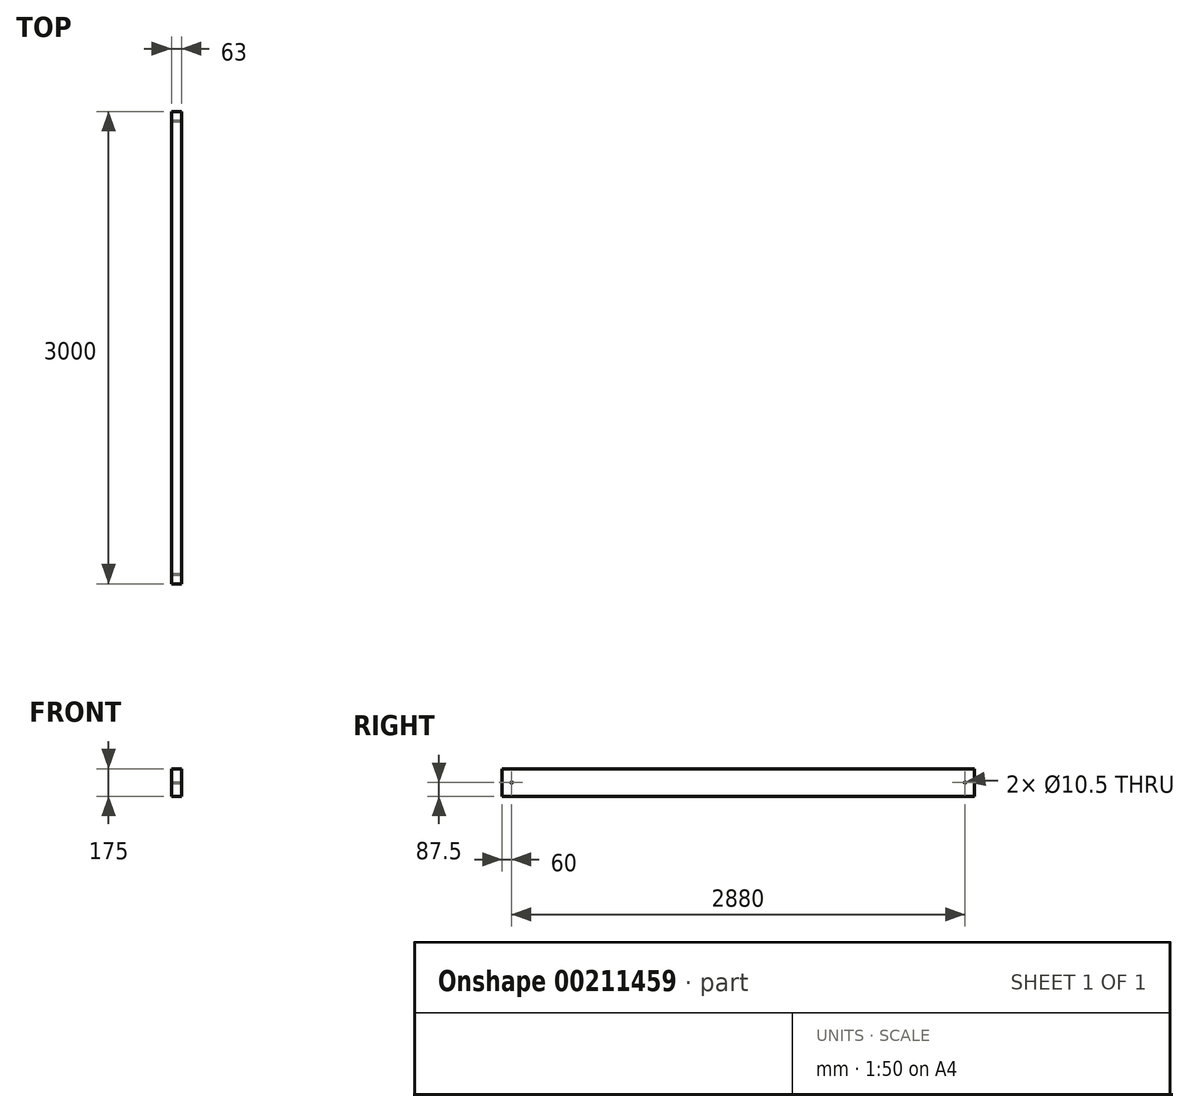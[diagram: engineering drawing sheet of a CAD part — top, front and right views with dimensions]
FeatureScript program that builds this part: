
annotation { "Feature Type Name" : "Feature", "Feature Type Description" : "" }
export const myFeature = defineFeature(function(context is Context, id is Id, definition is map)
    precondition{}
    {
        {
            var Q0;
            Q0=qCreatedBy(makeId("Front.planeOp"),FACE);
            var sketch = newSketch(context, id + "F0", { "sketchPlane" : qUnion([Q0])});
            skLineSegment(sketch, "E0.bottom", {"start": v(31.5, 87.5) * mm, "end": v(-31.5, 87.5) * mm});
            skLineSegment(sketch, "E0.top", {"start": v(31.5, -87.5) * mm, "end": v(-31.5, -87.5) * mm});
            skLineSegment(sketch, "E0.left", {"start": v(31.5, 87.5) * mm, "end": v(31.5, -87.5) * mm});
            skLineSegment(sketch, "E0.right", {"start": v(-31.5, 87.5) * mm, "end": v(-31.5, -87.5) * mm});
            skPoint(sketch, "E0.middle", {"position": v(0, 0) * mm});
            skSolve(sketch);
        }
        {
            var Q0;
            Q0=qSketchRegion(id+"F0",true);
            extrude(context, id + "F1", {"entities" : qUnion([Q0]), "depth" : 3000 * mm, "symmetric" : true});
        }
        {
            var Q0;
            Q0=makeQuery(id+"F1.opExtrude","SWEPT_FACE",FACE,{"disambiguationData":[OSD([sQuery(id+"F0.wireOp",EDGE,"E0.left")])]});
            var sketch = newSketch(context, id + "F2", { "sketchPlane" : qUnion([Q0])});
            skCircle(sketch, "E1", {"center": v(-1440, 0) * mm, "radius": 5.25 * mm});
            skCircle(sketch, "E2", {"center": v(1440, 0) * mm, "radius": 5.25 * mm});
            skSolve(sketch);
        }
        {
            var Q0;
            Q0=qSketchRegion(id+"F2",true);
            extrude(context, id + "F3", {"entities" : qUnion([Q0]), "operationType" : NewBodyOperationType.REMOVE, "endBound" : BoundingType.THROUGH_ALL, "oppositeDirection" : true, "depth" : 25 * mm});
        }
    });
